# Revit family: Gira_537626
name_source: partatom
category: Electrical Fixtures
revit_build: Autodesk Revit 2017 (Build: 20160225_1515(x64)
units: mm (PartAtom-declared; Revit-internal decimal feet)

## family parameters
Cut with Voids When Loaded = No
Host = Face
Maintain Annotation Orientation = Yes
Part Type = Normal
Room Calculation Point = No
Round Connector Dimension = Use Diameter
Shared = No

## types (1)
- S3000 motion detec.top 2.20 m Komfort BT System 55 c.alum.
    Available = No
    BIM (1) = https://media.stage.bim.site
    Category = Sensor element for movement sensor
    Data sheet (1) = https://katalog.gira.de
    Default Elevation = 1219 mm
    Description = S3000 mot.det.top 2.20m Kmf BT Sys55 CAl,System 3000 motion detector top unit 2.20 m Komfort BT,System 55,colour aluminium,Features:,- Automatic switching of lighting, depending on the movement of heat and ambient brightness.,- Operation with System 3000 switching or dimming insert or 3-wire auxiliary insert.,- Expansion of the detection range in combination with the 3-wire auxiliary insert.,- When connecting a System 3000 auxiliary insert with an operating top unit or mechanical button to the main unit, the lighting can be switched on or dimmed for the duration of the delay time.,- Device facilitates manual switchover between automatic, always-on and always-off.,With System 3000 switching insert:,- Short-term operation.,With System 3000 dimming insert:,- Switch on with the last brightness set, or a saved switch-on brightness.,- The switch-on brightness can only be saved permanently via the System 3000 auxiliary insert with operating top unit.,Functions with the Gira Bluetooth app:,- Set the brightness threshold.,- Individually adjustable sensitivity of the two sensors (0, 25, 50, 75, 100 %).,- Set the delay time.,- Override functions: Automatic mode, permanently on off, time-limited on off for 0.5 to 5 hours.,- Occupied-home simulation.,- Switch-off pre-warning.,- Day mode.,- Walking test.,- Switch on with the last brightness set, or a saved switch-on brightness in combination with a dimming insert.
    GTIN = 4010337050575
    HAN = 537626
    HeinzeBIM = https://bimportal.heinze.de
    Manufacturer = Gira
    Manufacturer URL = https://www.gira.de
    Model = Movement sensor
    Name = S3000 motion detec.top 2.20 m Komfort BT System 55 c.alum.
    URL = http://katalog.gira.de

## geometry (parser evidence)
native form markers: Blend x2, Sweep x3
no freeform markers — native parametric forms only
